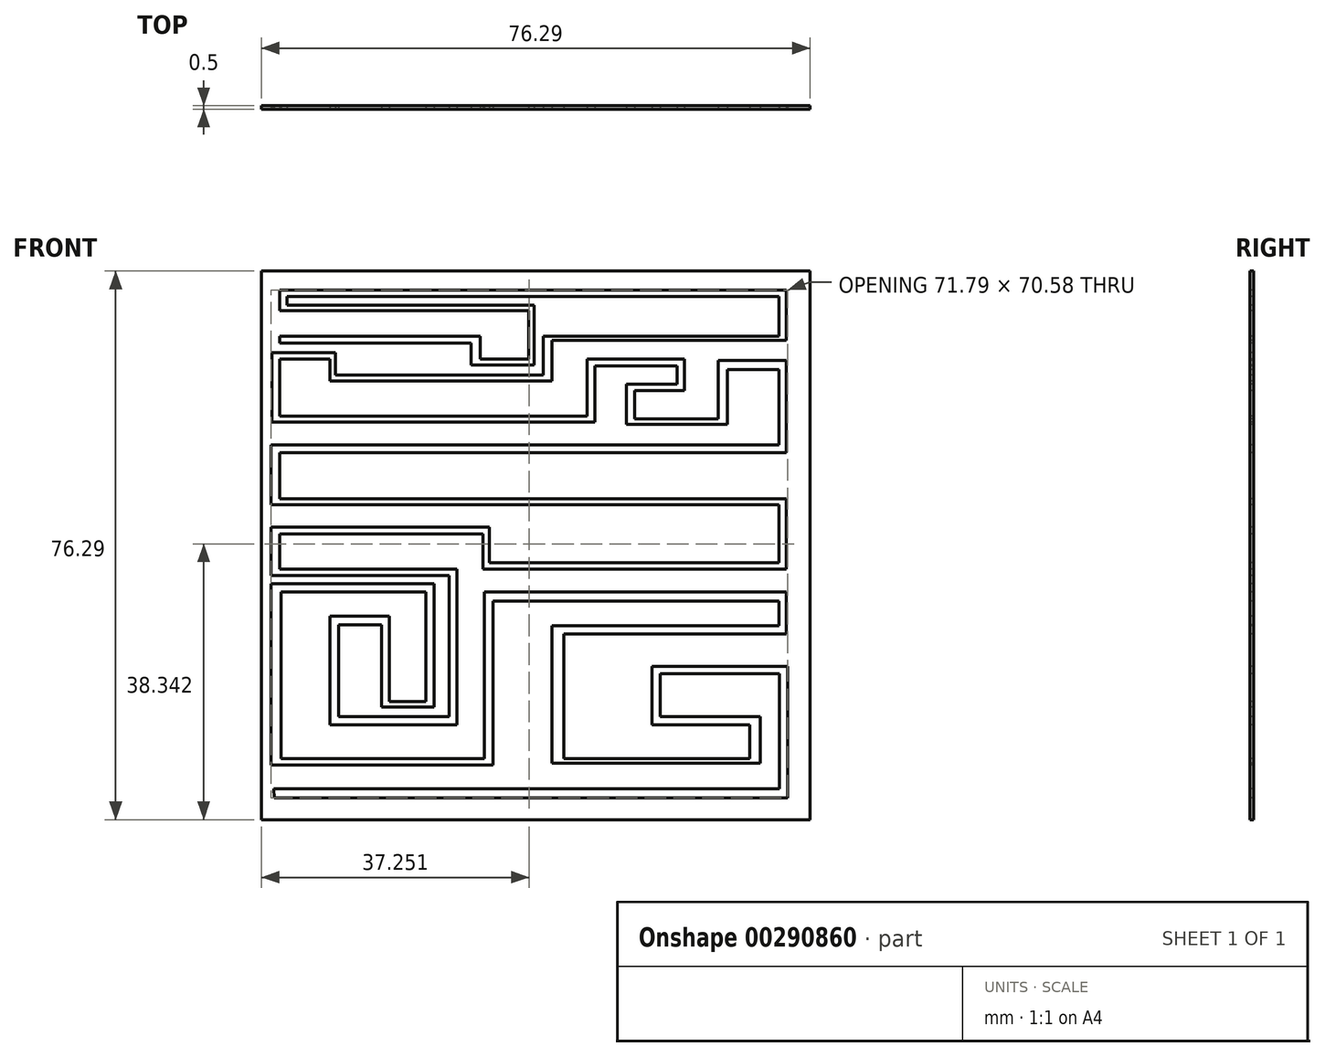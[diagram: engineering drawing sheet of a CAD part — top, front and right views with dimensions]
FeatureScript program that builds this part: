
annotation { "Feature Type Name" : "Feature", "Feature Type Description" : "" }
export const myFeature = defineFeature(function(context is Context, id is Id, definition is map)
    precondition{}
    {
        {
            var Q0;
            Q0=qCreatedBy(makeId("Front.planeOp"),FACE);
            var sketch = newSketch(context, id + "F0", { "sketchPlane" : qUnion([Q0])});
            skLineSegment(sketch, "E0.bottom", {"start": v(0, 0) * mm, "end": v(-76.3, 0) * mm});
            skLineSegment(sketch, "E0.top", {"start": v(0, 76.3) * mm, "end": v(-76.3, 76.3) * mm});
            skLineSegment(sketch, "E0.left", {"start": v(0, 0) * mm, "end": v(0, 76.3) * mm});
            skLineSegment(sketch, "E0.right", {"start": v(-76.3, 0) * mm, "end": v(-76.3, 76.3) * mm});
            skSolve(sketch);
        }
        {
            var Q0;
            Q0 = qSketchRegion(id + "F0", true);
            extrude(context, id + "F1", {"entities" : qUnion([Q0]), "depth" : .5 * mm});
        }
        {
            var Q0;
            Q0=makeQuery(id+"F1.opExtrude","CAP_FACE",FACE,{"disambiguationData":[OSD([sQuery(id+"F0.wireOp",EDGE,"E0.bottom"),sQuery(id+"F0.wireOp",EDGE,"E0.top"),sQuery(id+"F0.wireOp",EDGE,"E0.left"),sQuery(id+"F0.wireOp",EDGE,"E0.right")])],"isStart":false});
            var sketch = newSketch(context, id + "F2", { "sketchPlane" : qUnion([Q0])});
            skLineSegment(sketch, "E1", {"start": v(-74.47, 3.05) * mm, "end": v(-3.14, 3.05) * mm});
            skLineSegment(sketch, "E2", {"start": v(-3.14, 3.05) * mm, "end": v(-3.14, 21.3) * mm});
            skLineSegment(sketch, "E3", {"start": v(-3.14, 21.3) * mm, "end": v(-21.96, 21.3) * mm});
            skLineSegment(sketch, "E4", {"start": v(-21.96, 21.3) * mm, "end": v(-21.96, 13.22) * mm});
            skLineSegment(sketch, "E5", {"start": v(-21.96, 13.22) * mm, "end": v(-8.41, 13.22) * mm});
            skLineSegment(sketch, "E6", {"start": v(-8.41, 13.22) * mm, "end": v(-8.41, 8.51) * mm});
            skLineSegment(sketch, "E7", {"start": v(-8.41, 8.51) * mm, "end": v(-34.2, 8.51) * mm});
            skLineSegment(sketch, "E8", {"start": v(-34.2, 8.51) * mm, "end": v(-34.2, 25.83) * mm});
            skLineSegment(sketch, "E9", {"start": v(-34.2, 25.83) * mm, "end": v(-3.33, 25.83) * mm});
            skLineSegment(sketch, "E10", {"start": v(-3.33, 25.83) * mm, "end": v(-3.33, 31.66) * mm});
            skLineSegment(sketch, "E11", {"start": v(-3.33, 31.66) * mm, "end": v(-45.3, 31.66) * mm});
            skLineSegment(sketch, "E12", {"start": v(-45.3, 31.66) * mm, "end": v(-45.3, 8.51) * mm});
            skLineSegment(sketch, "E13", {"start": v(-45.3, 8.51) * mm, "end": v(-73.53, 8.51) * mm});
            skLineSegment(sketch, "E14", {"start": v(-73.53, 8.51) * mm, "end": v(-73.53, 31.66) * mm});
            skLineSegment(sketch, "E15", {"start": v(-73.53, 31.66) * mm, "end": v(-53.4, 31.66) * mm});
            skLineSegment(sketch, "E16", {"start": v(-53.4, 31.66) * mm, "end": v(-53.4, 16.42) * mm});
            skLineSegment(sketch, "E17", {"start": v(-53.4, 16.42) * mm, "end": v(-58.48, 16.42) * mm});
            skLineSegment(sketch, "E18", {"start": v(-58.48, 16.42) * mm, "end": v(-58.48, 28.27) * mm});
            skLineSegment(sketch, "E19", {"start": v(-58.48, 28.27) * mm, "end": v(-66.76, 28.27) * mm});
            skLineSegment(sketch, "E20", {"start": v(-66.76, 28.27) * mm, "end": v(-66.76, 13.22) * mm});
            skLineSegment(sketch, "E21", {"start": v(-66.76, 13.22) * mm, "end": v(-49.07, 13.22) * mm});
            skLineSegment(sketch, "E22", {"start": v(-49.07, 13.22) * mm, "end": v(-49.07, 34.86) * mm});
            skLineSegment(sketch, "E23", {"start": v(-49.07, 34.86) * mm, "end": v(-73.72, 34.86) * mm});
            skLineSegment(sketch, "E24", {"start": v(-73.72, 34.86) * mm, "end": v(-73.72, 39.75) * mm});
            skLineSegment(sketch, "E25", {"start": v(-73.72, 39.75) * mm, "end": v(-45.5, 39.75) * mm});
            skLineSegment(sketch, "E26", {"start": v(-45.5, 39.75) * mm, "end": v(-45.5, 34.86) * mm});
            skLineSegment(sketch, "E27", {"start": v(-45.5, 34.86) * mm, "end": v(-3.33, 34.86) * mm});
            skLineSegment(sketch, "E28", {"start": v(-3.33, 34.86) * mm, "end": v(-3.33, 44.65) * mm});
            skLineSegment(sketch, "E29", {"start": v(-3.33, 44.65) * mm, "end": v(-73.72, 44.65) * mm});
            skLineSegment(sketch, "E30", {"start": v(-73.72, 44.65) * mm, "end": v(-73.72, 51.05) * mm});
            skLineSegment(sketch, "E31", {"start": v(-73.72, 51.05) * mm, "end": v(-3.33, 51.05) * mm});
            skLineSegment(sketch, "E32", {"start": v(-3.33, 51.05) * mm, "end": v(-3.33, 63.84) * mm});
            skLineSegment(sketch, "E33", {"start": v(-3.33, 63.84) * mm, "end": v(-12.74, 63.84) * mm});
            skLineSegment(sketch, "E34", {"start": v(-12.74, 63.84) * mm, "end": v(-12.74, 55.75) * mm});
            skLineSegment(sketch, "E35", {"start": v(-12.74, 55.75) * mm, "end": v(-24.41, 55.75) * mm});
            skLineSegment(sketch, "E36", {"start": v(-24.41, 55.75) * mm, "end": v(-24.41, 59.7) * mm});
            skLineSegment(sketch, "E37", {"start": v(-24.41, 59.7) * mm, "end": v(-17.45, 59.7) * mm});
            skLineSegment(sketch, "E38", {"start": v(-17.45, 59.7) * mm, "end": v(-17.45, 64.03) * mm});
            skLineSegment(sketch, "E39", {"start": v(-17.45, 64.03) * mm, "end": v(-31, 64.03) * mm});
            skLineSegment(sketch, "E40", {"start": v(-31, 64.03) * mm, "end": v(-31, 56.13) * mm});
            skLineSegment(sketch, "E41", {"start": v(-31, 56.13) * mm, "end": v(-73.72, 56.13) * mm});
            skLineSegment(sketch, "E42", {"start": v(-73.72, 56.13) * mm, "end": v(-73.72, 64.03) * mm});
            skLineSegment(sketch, "E43", {"start": v(-73.72, 64.03) * mm, "end": v(-66.76, 64.03) * mm});
            skLineSegment(sketch, "E44", {"start": v(-66.76, 64.03) * mm, "end": v(-66.76, 61.02) * mm});
            skLineSegment(sketch, "E45", {"start": v(-66.76, 61.02) * mm, "end": v(-35.9, 61.02) * mm});
            skLineSegment(sketch, "E46", {"start": v(-35.9, 61.02) * mm, "end": v(-35.9, 66.67) * mm});
            skLineSegment(sketch, "E47", {"start": v(-35.9, 66.67) * mm, "end": v(-3.33, 66.67) * mm});
            skLineSegment(sketch, "E48", {"start": v(-3.33, 66.67) * mm, "end": v(-3.33, 73.63) * mm});
            skLineSegment(sketch, "E49", {"start": v(-3.33, 73.63) * mm, "end": v(-73.72, 73.63) * mm});
            skLineSegment(sketch, "E50", {"start": v(-73.72, 73.63) * mm, "end": v(-73.72, 70.8) * mm});
            skLineSegment(sketch, "E51", {"start": v(-73.72, 70.8) * mm, "end": v(-39.1, 70.8) * mm});
            skLineSegment(sketch, "E52", {"start": v(-39.1, 70.8) * mm, "end": v(-39.1, 64.03) * mm});
            skLineSegment(sketch, "E53", {"start": v(-39.1, 64.03) * mm, "end": v(-45.87, 64.03) * mm});
            skLineSegment(sketch, "E54", {"start": v(-45.87, 64.03) * mm, "end": v(-45.87, 67.23) * mm});
            skLineSegment(sketch, "E55", {"start": v(-45.87, 67.23) * mm, "end": v(-73.72, 67.23) * mm});
            skLineSegment(sketch, "E56", {"start": v(-73.72, 67.23) * mm, "end": v(-73.72, 66.29) * mm});
            skLineSegment(sketch, "E57", {"start": v(-73.72, 66.29) * mm, "end": v(-47.13, 66.29) * mm});
            skLineSegment(sketch, "E58", {"start": v(-47.13, 66.29) * mm, "end": v(-47.13, 63.22) * mm});
            skLineSegment(sketch, "E59", {"start": v(-47.13, 63.22) * mm, "end": v(-38.35, 63.22) * mm});
            skLineSegment(sketch, "E60", {"start": v(-38.35, 63.22) * mm, "end": v(-38.35, 71.57) * mm});
            skLineSegment(sketch, "E61", {"start": v(-38.35, 71.57) * mm, "end": v(-72.71, 71.57) * mm});
            skLineSegment(sketch, "E62", {"start": v(-72.71, 71.57) * mm, "end": v(-72.71, 72.74) * mm});
            skLineSegment(sketch, "E63", {"start": v(-72.71, 72.74) * mm, "end": v(-4.3, 72.74) * mm});
            skLineSegment(sketch, "E64", {"start": v(-4.3, 72.74) * mm, "end": v(-4.3, 67.23) * mm});
            skLineSegment(sketch, "E65", {"start": v(-4.3, 67.23) * mm, "end": v(-37.08, 67.23) * mm});
            skLineSegment(sketch, "E66", {"start": v(-37.08, 67.23) * mm, "end": v(-37.08, 61.85) * mm});
            skLineSegment(sketch, "E67", {"start": v(-37.08, 61.85) * mm, "end": v(-65.95, 61.85) * mm});
            skLineSegment(sketch, "E68", {"start": v(-65.95, 61.85) * mm, "end": v(-65.95, 64.91) * mm});
            skLineSegment(sketch, "E69", {"start": v(-65.95, 64.91) * mm, "end": v(-74.83, 64.91) * mm});
            skLineSegment(sketch, "E70", {"start": v(-74.83, 64.91) * mm, "end": v(-74.83, 55.3) * mm});
            skLineSegment(sketch, "E71", {"start": v(-74.83, 55.3) * mm, "end": v(-29.9, 55.3) * mm});
            skLineSegment(sketch, "E72", {"start": v(-29.9, 55.3) * mm, "end": v(-29.9, 63.12) * mm});
            skLineSegment(sketch, "E73", {"start": v(-29.9, 63.12) * mm, "end": v(-18.47, 63.12) * mm});
            skLineSegment(sketch, "E74", {"start": v(-18.47, 63.12) * mm, "end": v(-18.47, 60.58) * mm});
            skLineSegment(sketch, "E75", {"start": v(-18.47, 60.58) * mm, "end": v(-25.56, 60.58) * mm});
            skLineSegment(sketch, "E76", {"start": v(-25.56, 60.58) * mm, "end": v(-25.56, 54.97) * mm});
            skLineSegment(sketch, "E77", {"start": v(-25.56, 54.97) * mm, "end": v(-11.5, 54.97) * mm});
            skLineSegment(sketch, "E78", {"start": v(-11.5, 54.97) * mm, "end": v(-11.5, 62.59) * mm});
            skLineSegment(sketch, "E79", {"start": v(-11.5, 62.59) * mm, "end": v(-4.3, 62.59) * mm});
            skLineSegment(sketch, "E80", {"start": v(-4.3, 62.59) * mm, "end": v(-4.3, 52.12) * mm});
            skLineSegment(sketch, "E81", {"start": v(-4.3, 52.12) * mm, "end": v(-74.94, 52.12) * mm});
            skLineSegment(sketch, "E82", {"start": v(-74.94, 52.12) * mm, "end": v(-74.94, 43.77) * mm});
            skLineSegment(sketch, "E83", {"start": v(-74.94, 43.77) * mm, "end": v(-4.3, 43.77) * mm});
            skLineSegment(sketch, "E84", {"start": v(-4.3, 43.77) * mm, "end": v(-4.3, 35.73) * mm});
            skLineSegment(sketch, "E85", {"start": v(-4.3, 35.73) * mm, "end": v(-44.6, 35.73) * mm});
            skLineSegment(sketch, "E86", {"start": v(-44.6, 35.73) * mm, "end": v(-44.6, 40.7) * mm});
            skLineSegment(sketch, "E87", {"start": v(-44.6, 40.7) * mm, "end": v(-74.94, 40.7) * mm});
            skLineSegment(sketch, "E88", {"start": v(-74.94, 40.7) * mm, "end": v(-74.94, 33.93) * mm});
            skLineSegment(sketch, "E89", {"start": v(-74.94, 33.93) * mm, "end": v(-50.2, 33.93) * mm});
            skLineSegment(sketch, "E90", {"start": v(-50.2, 33.93) * mm, "end": v(-50.2, 14.35) * mm});
            skLineSegment(sketch, "E91", {"start": v(-50.2, 14.35) * mm, "end": v(-65.56, 14.35) * mm});
            skLineSegment(sketch, "E92", {"start": v(-65.56, 14.35) * mm, "end": v(-65.56, 27.09) * mm});
            skLineSegment(sketch, "E93", {"start": v(-65.56, 27.09) * mm, "end": v(-59.59, 27.09) * mm});
            skLineSegment(sketch, "E94", {"start": v(-59.59, 27.09) * mm, "end": v(-59.59, 15.68) * mm});
            skLineSegment(sketch, "E95", {"start": v(-59.59, 15.68) * mm, "end": v(-52.3, 15.68) * mm});
            skLineSegment(sketch, "E96", {"start": v(-52.3, 15.68) * mm, "end": v(-52.3, 32.8) * mm});
            skLineSegment(sketch, "E97", {"start": v(-52.3, 32.8) * mm, "end": v(-74.94, 32.8) * mm});
            skLineSegment(sketch, "E98", {"start": v(-74.94, 32.8) * mm, "end": v(-74.94, 7.59) * mm});
            skLineSegment(sketch, "E99", {"start": v(-74.94, 7.59) * mm, "end": v(-44.07, 7.59) * mm});
            skLineSegment(sketch, "E100", {"start": v(-44.07, 7.59) * mm, "end": v(-44.07, 30.4) * mm});
            skLineSegment(sketch, "E101", {"start": v(-44.07, 30.4) * mm, "end": v(-4.3, 30.4) * mm});
            skLineSegment(sketch, "E102", {"start": v(-4.3, 30.4) * mm, "end": v(-4.3, 26.95) * mm});
            skLineSegment(sketch, "E103", {"start": v(-4.3, 26.95) * mm, "end": v(-35.9, 26.95) * mm});
            skLineSegment(sketch, "E104", {"start": v(-35.9, 26.95) * mm, "end": v(-35.9, 7.86) * mm});
            skLineSegment(sketch, "E105", {"start": v(-35.9, 7.86) * mm, "end": v(-6.93, 7.86) * mm});
            skLineSegment(sketch, "E106", {"start": v(-6.93, 7.86) * mm, "end": v(-6.93, 14.35) * mm});
            skLineSegment(sketch, "E107", {"start": v(-6.93, 14.35) * mm, "end": v(-20.86, 14.35) * mm});
            skLineSegment(sketch, "E108", {"start": v(-20.86, 14.35) * mm, "end": v(-20.86, 20.32) * mm});
            skLineSegment(sketch, "E109", {"start": v(-20.86, 20.32) * mm, "end": v(-4.28, 20.32) * mm});
            skLineSegment(sketch, "E110", {"start": v(-4.28, 20.32) * mm, "end": v(-4.28, 4.27) * mm});
            skLineSegment(sketch, "E111", {"start": v(-4.28, 4.27) * mm, "end": v(-74.57, 4.27) * mm});
            skLineSegment(sketch, "E112", {"start": v(-74.57, 4.27) * mm, "end": v(-74.47, 3.05) * mm});
            skSolve(sketch);
        }
        {
            var Q0;
            Q0 = qSketchRegion(id + "F2", true);
            extrude(context, id + "F3", {"entities" : qUnion([Q0]), "operationType" : NewBodyOperationType.REMOVE, "oppositeDirection" : true, "depth" : .5 * mm});
        }
    });
